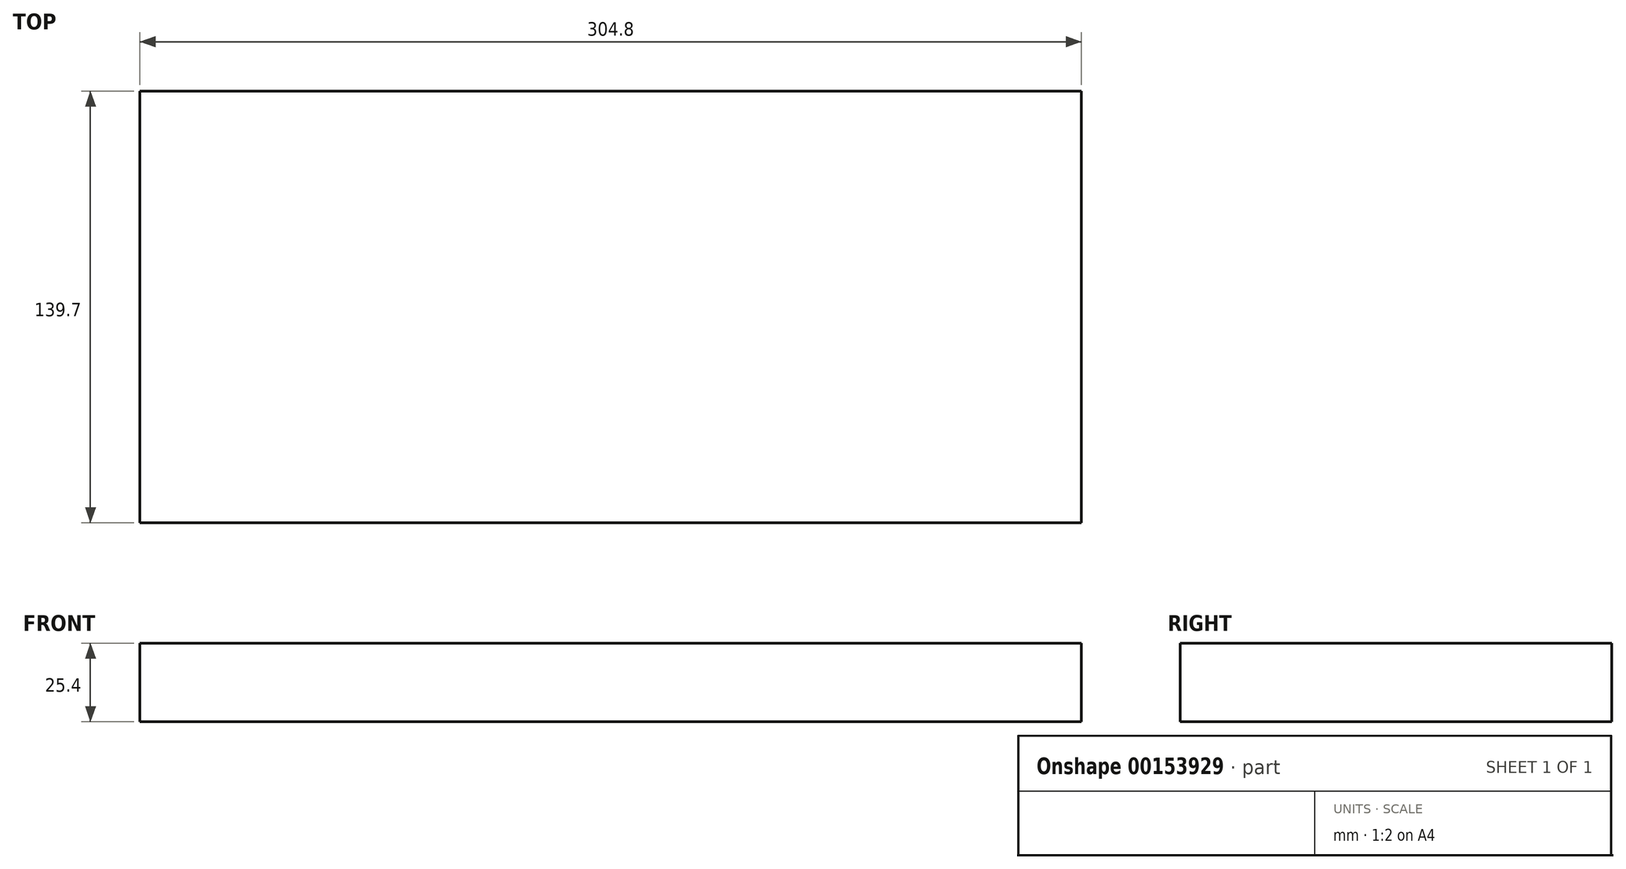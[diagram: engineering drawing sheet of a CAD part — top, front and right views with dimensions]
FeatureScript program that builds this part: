
annotation { "Feature Type Name" : "Feature", "Feature Type Description" : "" }
export const myFeature = defineFeature(function(context is Context, id is Id, definition is map)
    precondition{}
    {
        {
            var Q0;
            Q0=qCreatedBy(makeId("Top.planeOp"),FACE);
            var sketch = newSketch(context, id + "F0", { "sketchPlane" : qUnion([Q0])});
            skLineSegment(sketch, "E0.bottom", {"start": v(152.4, -69.85) * mm, "end": v(-152.4, -69.85) * mm});
            skLineSegment(sketch, "E0.top", {"start": v(152.4, 69.85) * mm, "end": v(-152.4, 69.85) * mm});
            skLineSegment(sketch, "E0.left", {"start": v(152.4, -69.85) * mm, "end": v(152.4, 69.85) * mm});
            skLineSegment(sketch, "E0.right", {"start": v(-152.4, -69.85) * mm, "end": v(-152.4, 69.85) * mm});
            skPoint(sketch, "E0.middle", {"position": v(0, 0) * mm});
            skSolve(sketch);
        }
        {
            var Q0;
            Q0=makeQuery(id+"F0.imprint","IMPRINT",FACE,{"disambiguationData":[TD([[makeQuery(id+"F0.imprint","IMPRINT",EDGE,{"derivedFrom":sQuery(id+"F0.wireOp",EDGE,"E0.bottom")}),-1.0]])]});
            extrude(context, id + "F1", {"entities" : qUnion([Q0]), "depth" : 25.4 * mm});
        }
    });
